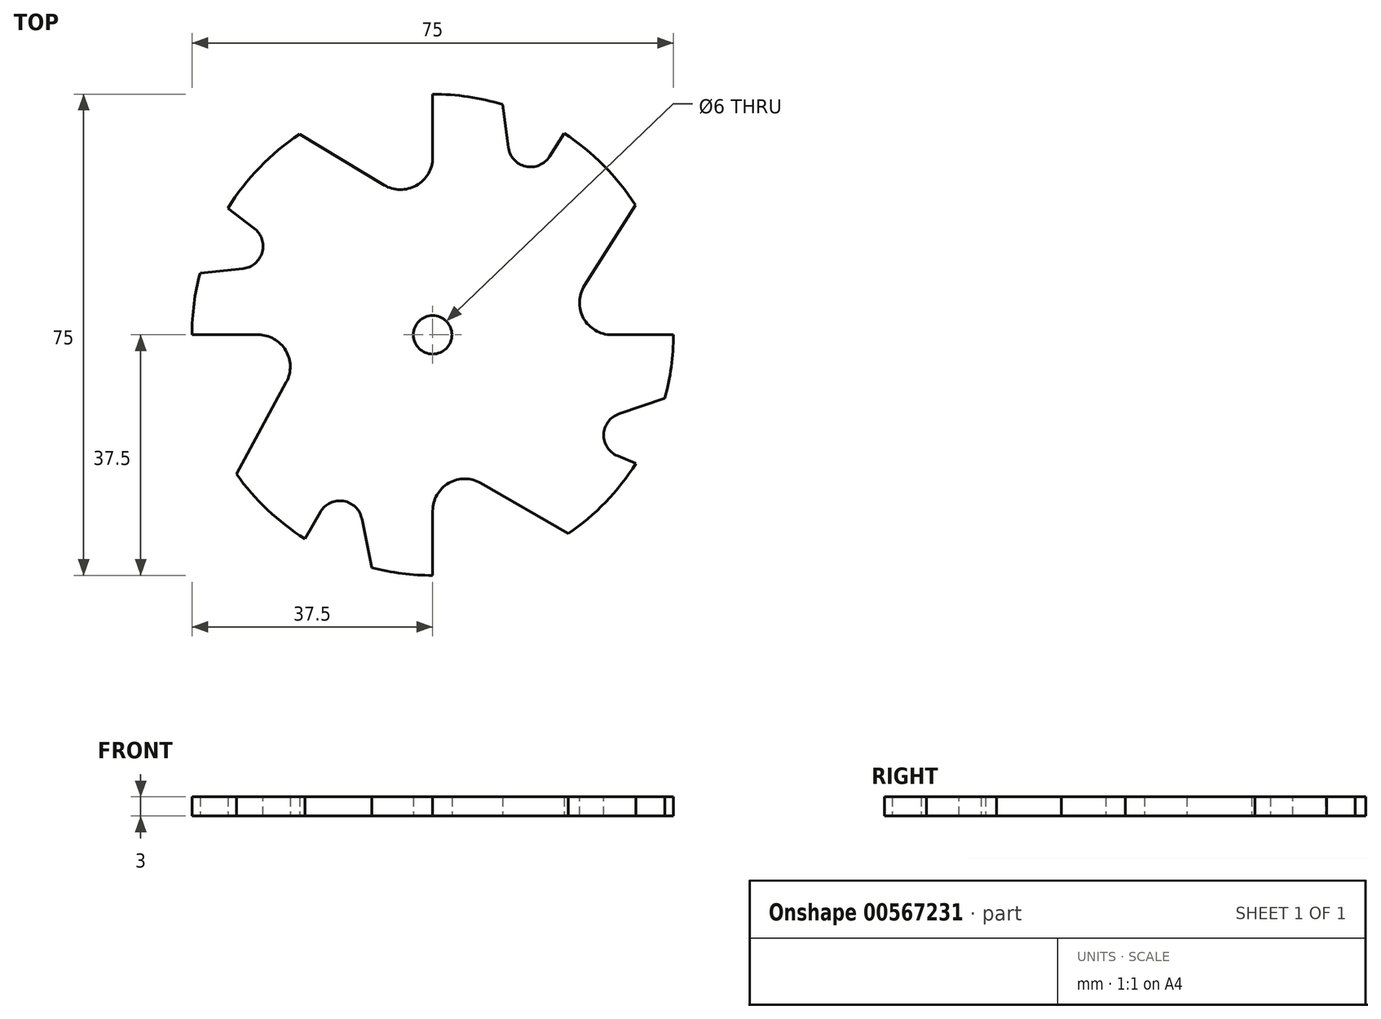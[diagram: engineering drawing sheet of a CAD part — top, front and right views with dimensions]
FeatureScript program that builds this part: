
annotation { "Feature Type Name" : "Feature", "Feature Type Description" : "" }
export const myFeature = defineFeature(function(context is Context, id is Id, definition is map)
    precondition{}
    {
        {
            var Q0;
            Q0=qCreatedBy(makeId("Top.planeOp"),FACE);
            var sketch = newSketch(context, id + "F0", { "sketchPlane" : qUnion([Q0])});
            skLineSegment(sketch, "E0.bottom", {"start": v(0, 0) * mm, "end": v(75, 0) * mm, "construction": true});
            skLineSegment(sketch, "E0.top", {"start": v(0, 75) * mm, "end": v(75, 75) * mm, "construction": true});
            skLineSegment(sketch, "E0.left", {"start": v(0, 0) * mm, "end": v(0, 75) * mm, "construction": true});
            skLineSegment(sketch, "E0.right", {"start": v(75, 0) * mm, "end": v(75, 75) * mm, "construction": true});
            skCircle(sketch, "E1", {"center": v(37.5, 37.5) * mm, "radius": 3 * mm});
            skCircle(sketch, "E2", {"center": v(37.5, 37.5) * mm, "radius": 37.5 * mm});
            skLineSegment(sketch, "E3", {"start": v(0, 37.5) * mm, "end": v(18.7, 37.5) * mm});
            skPoint(sketch, "E4.endSnap0", {"position": v(75, 37.5) * mm});
            skLineSegment(sketch, "E5", {"start": v(37.5, 75) * mm, "end": v(37.5, 56.3) * mm});
            skLineSegment(sketch, "E6", {"start": v(16.75, 68.74) * mm, "end": v(37.5, 56.3) * mm});
            skLineSegment(sketch, "E7", {"start": v(75, 37.5) * mm, "end": v(56.3, 37.5) * mm});
            skLineSegment(sketch, "E8", {"start": v(56.3, 37.5) * mm, "end": v(69.08, 57.72) * mm});
            skLineSegment(sketch, "E9", {"start": v(6.94, 15.77) * mm, "end": v(18.7, 37.5) * mm});
            skLineSegment(sketch, "E10", {"start": v(37.5, 0) * mm, "end": v(37.5, 18.7) * mm});
            skLineSegment(sketch, "E11", {"start": v(58.64, 6.53) * mm, "end": v(37.5, 18.7) * mm});
            skLineSegment(sketch, "E12", {"start": v(5.59, 57.2) * mm, "end": v(16.75, 48.75) * mm});
            skLineSegment(sketch, "E13", {"start": v(16.75, 48.75) * mm, "end": v(1.25, 47.12) * mm});
            skLineSegment(sketch, "E14", {"start": v(58, 68.9) * mm, "end": v(50.51, 57.07) * mm});
            skLineSegment(sketch, "E15", {"start": v(50.51, 57.07) * mm, "end": v(48.43, 73.37) * mm});
            skLineSegment(sketch, "E16", {"start": v(17.58, 5.73) * mm, "end": v(24.64, 17.82) * mm});
            skLineSegment(sketch, "E17", {"start": v(24.64, 17.82) * mm, "end": v(28.01, 1.22) * mm});
            skLineSegment(sketch, "E18", {"start": v(69.18, 17.43) * mm, "end": v(57.72, 22.2) * mm});
            skLineSegment(sketch, "E19", {"start": v(57.72, 22.2) * mm, "end": v(73.67, 27.58) * mm});
            skSolve(sketch);
        }
        {
            var Q0;
            Q0=makeQuery(id+"F0.imprint","IMPRINT",FACE,{"disambiguationData":[TD([[makeQuery(id+"F0.imprint","IMPRINT",EDGE,{"derivedFrom":sQuery(id+"F0.wireOp",EDGE,"E1")}),-1.0]])]});
            extrude(context, id + "F1", {"entities" : qUnion([Q0]), "depth" : 3 * mm, "offsetDistance" : 25 * mm});
        }
        {
            var Q0;
            Q0=makeQuery(id+"F1.opExtrude","SWEPT_EDGE",EDGE,{"disambiguationData":[OSD([sQuery(id+"F0.wireOp",EDGE,"E10"),sQuery(id+"F0.wireOp",EDGE,"E11")])]});
            fillet(context, id + "F2", {"entities" : qUnion([Q0]), "radius" : 5 * mm, "tangentPropagation" : true, "allowEdgeOverflow" : false});
        }
        {
            var Q0;
            Q0=makeQuery(id+"F1.opExtrude","SWEPT_EDGE",EDGE,{"disambiguationData":[OSD([sQuery(id+"F0.wireOp",EDGE,"E7"),sQuery(id+"F0.wireOp",EDGE,"E8")])]});
            fillet(context, id + "F3", {"entities" : qUnion([Q0]), "radius" : 5 * mm, "tangentPropagation" : true, "allowEdgeOverflow" : false});
        }
        {
            var Q0;
            Q0=makeQuery(id+"F1.opExtrude","SWEPT_EDGE",EDGE,{"disambiguationData":[OSD([sQuery(id+"F0.wireOp",EDGE,"E3"),sQuery(id+"F0.wireOp",EDGE,"E9")])]});
            fillet(context, id + "F4", {"entities" : qUnion([Q0]), "radius" : 5 * mm, "tangentPropagation" : true, "allowEdgeOverflow" : false});
        }
        {
            var Q0;
            Q0=makeQuery(id+"F1.opExtrude","SWEPT_EDGE",EDGE,{"disambiguationData":[OSD([sQuery(id+"F0.wireOp",EDGE,"E5"),sQuery(id+"F0.wireOp",EDGE,"E6")])]});
            fillet(context, id + "F5", {"entities" : qUnion([Q0]), "radius" : 5 * mm, "tangentPropagation" : true, "allowEdgeOverflow" : false});
        }
        {
            var Q0;
            Q0=makeQuery(id+"F1.opExtrude","SWEPT_EDGE",EDGE,{"disambiguationData":[OSD([sQuery(id+"F0.wireOp",EDGE,"E16"),sQuery(id+"F0.wireOp",EDGE,"E17")])]});
            fillet(context, id + "F6", {"entities" : qUnion([Q0]), "radius" : 3.5 * mm, "tangentPropagation" : true, "allowEdgeOverflow" : false});
        }
        {
            var Q0;
            Q0=makeQuery(id+"F1.opExtrude","SWEPT_EDGE",EDGE,{"disambiguationData":[OSD([sQuery(id+"F0.wireOp",EDGE,"E18"),sQuery(id+"F0.wireOp",EDGE,"E19")])]});
            fillet(context, id + "F7", {"entities" : qUnion([Q0]), "radius" : 3.5 * mm, "tangentPropagation" : true, "allowEdgeOverflow" : false});
        }
        {
            var Q0;
            Q0=makeQuery(id+"F1.opExtrude","SWEPT_EDGE",EDGE,{"disambiguationData":[OSD([sQuery(id+"F0.wireOp",EDGE,"E14"),sQuery(id+"F0.wireOp",EDGE,"E15")])]});
            fillet(context, id + "F8", {"entities" : qUnion([Q0]), "radius" : 3.5 * mm, "tangentPropagation" : true, "allowEdgeOverflow" : false});
        }
        {
            var Q0;
            Q0=makeQuery(id+"F1.opExtrude","SWEPT_EDGE",EDGE,{"disambiguationData":[OSD([sQuery(id+"F0.wireOp",EDGE,"E12"),sQuery(id+"F0.wireOp",EDGE,"E13")])]});
            fillet(context, id + "F9", {"entities" : qUnion([Q0]), "radius" : 3.5 * mm, "tangentPropagation" : true, "allowEdgeOverflow" : false});
        }
    });
